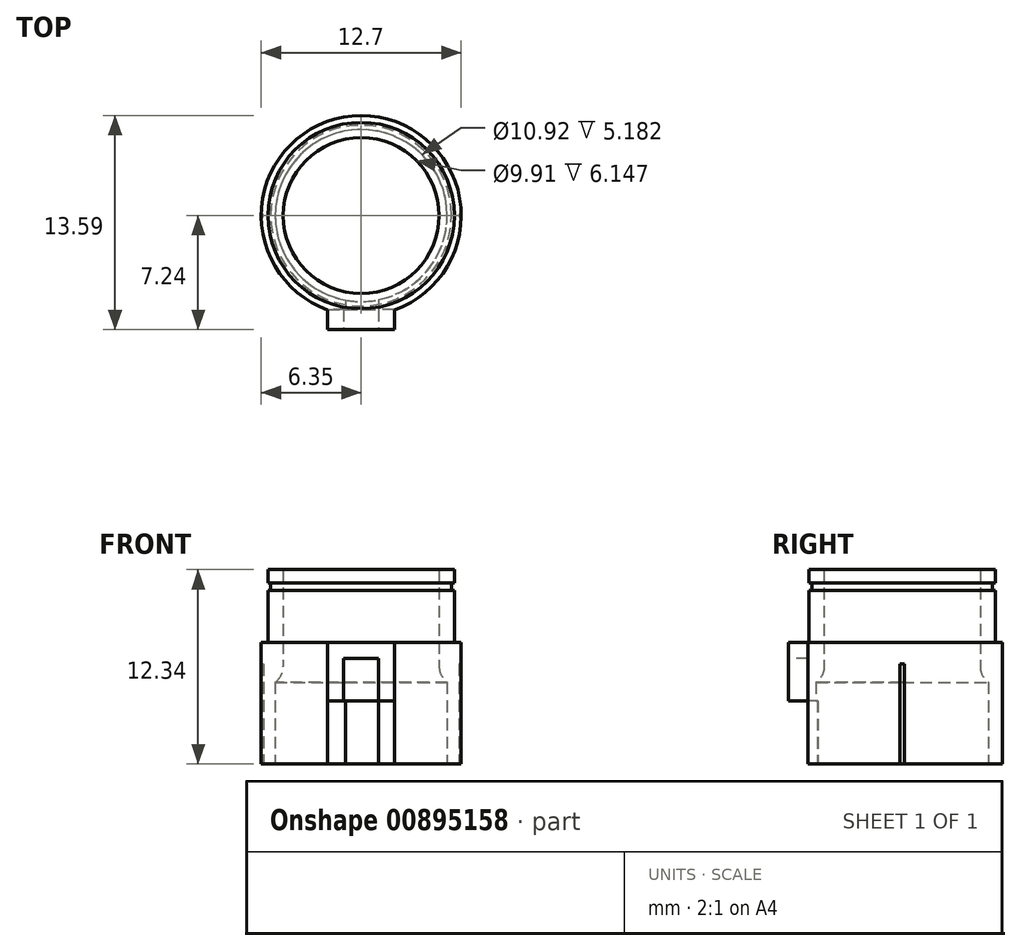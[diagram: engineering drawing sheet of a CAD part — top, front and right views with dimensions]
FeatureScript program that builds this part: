
annotation { "Feature Type Name" : "Feature", "Feature Type Description" : "" }
export const myFeature = defineFeature(function(context is Context, id is Id, definition is map)
    precondition{}
    {
        {
            var Q0;
            Q0=qCreatedBy(makeId("Top.planeOp"),FACE);
            var sketch = newSketch(context, id + "F0", { "sketchPlane" : qUnion([Q0])});
            skCircle(sketch, "E0", {"center": v(0, 0) * mm, "radius": 6.35 * mm});
            skLineSegment(sketch, "E1.bottom", {"start": v(2.12, -5.46) * mm, "end": v(-2.12, -5.46) * mm});
            skLineSegment(sketch, "E1.top", {"start": v(2.12, -7.24) * mm, "end": v(-2.12, -7.24) * mm});
            skLineSegment(sketch, "E1.left", {"start": v(2.12, -5.46) * mm, "end": v(2.12, -7.24) * mm});
            skLineSegment(sketch, "E1.right", {"start": v(-2.12, -5.46) * mm, "end": v(-2.12, -7.24) * mm});
            skPoint(sketch, "E1.middle", {"position": v(0, -6.35) * mm});
            skCircle(sketch, "E2", {"center": v(0, 0) * mm, "radius": 5.46 * mm});
            skSolve(sketch);
        }
        {
            var Q0;
            {var subQ5=sQuery(id+"F0.wireOp",EDGE,"E1.top");Q0=makeQuery(id+"F0.imprint","IMPRINT",FACE,{"disambiguationData":[TD([[makeQuery(id+"F0.imprint","IMPRINT",EDGE,{"derivedFrom":subQ5}),-1.0]])]});}
            var Q1;
            {var subQ4=sQuery(id+"F0.wireOp",EDGE,"E1.left");var subQ6=sQuery(id+"F0.wireOp",EDGE,"E0");var subQ7=makeQuery(id+"F0.imprint","INTERSECT",VERTEX,{"derivedFrom":[subQ6,subQ4]});Q1=makeQuery(id+"F0.imprint","IMPRINT",FACE,{"disambiguationData":[TD([[makeQuery(id+"F0.imprint","IMPRINT",EDGE,{"disambiguationData":[TD([[subQ7,1.0]])],"derivedFrom":subQ6}),1.0]])]});}
            var Q2;
            {var subQ7=sQuery(id+"F0.wireOp",EDGE,"E2");Q2=makeQuery(id+"F0.imprint","IMPRINT",FACE,{"disambiguationData":[TD([[makeQuery(id+"F0.imprint","IMPRINT",EDGE,{"derivedFrom":subQ7}),-1.0]])]});}
            extrude(context, id + "F1", {"entities" : qUnion([Q0, Q1, Q2]), "depth" : 7.72 * mm, "offsetDistance" : 25.4 * mm});
        }
        {
            var Q0;
            Q0=makeQuery(id+"F1.opExtrude","SWEPT_FACE",FACE,{"disambiguationData":[OSD([sQuery(id+"F0.wireOp",EDGE,"E1.top")])]});
            var sketch = newSketch(context, id + "F2", { "sketchPlane" : qUnion([Q0])});
            skLineSegment(sketch, "E3.bottom", {"start": v(-1.1, 0) * mm, "end": v(1.1, 0) * mm});
            skLineSegment(sketch, "E3.top", {"start": v(-1.1, 6.7) * mm, "end": v(1.1, 6.7) * mm});
            skLineSegment(sketch, "E3.left", {"start": v(-1.1, 0) * mm, "end": v(-1.1, 6.7) * mm});
            skLineSegment(sketch, "E3.right", {"start": v(1.1, 0) * mm, "end": v(1.1, 6.7) * mm});
            skLineSegment(sketch, "E4.bottom", {"start": v(-2.12, 4.01) * mm, "end": v(2.12, 4.01) * mm});
            skLineSegment(sketch, "E4.top", {"start": v(-2.12, 0) * mm, "end": v(2.12, 0) * mm});
            skLineSegment(sketch, "E4.left", {"start": v(-2.12, 4.01) * mm, "end": v(-2.12, 0) * mm});
            skLineSegment(sketch, "E4.right", {"start": v(2.12, 4.01) * mm, "end": v(2.12, 0) * mm});
            skSolve(sketch);
        }
        {
            var Q0;
            Q0 = qSketchRegion(id + "F2", true);
            extrude(context, id + "F3", {"entities" : qUnion([Q0]), "operationType" : NewBodyOperationType.REMOVE, "oppositeDirection" : true, "depth" : 1.27 * mm, "offsetDistance" : 25.4 * mm});
        }
        {
            var Q0;
            Q0=makeQuery(id+"F1.opExtrude","CAP_FACE",FACE,{"disambiguationData":[OSD([sQuery(id+"F0.wireOp",EDGE,"E0"),sQuery(id+"F0.wireOp",EDGE,"E1.top"),sQuery(id+"F0.wireOp",EDGE,"E1.left"),sQuery(id+"F0.wireOp",EDGE,"E1.right"),sQuery(id+"F0.wireOp",EDGE,"E2")])],"isStart":true});
            var sketch = newSketch(context, id + "F4", { "sketchPlane" : qUnion([Q0])});
            skCircle(sketch, "E5", {"center": v(-6.35, 0) * mm, "radius": 0.14 * mm});
            skCircle(sketch, "E6", {"center": v(6.35, 0) * mm, "radius": 0.14 * mm});
            skSolve(sketch);
        }
        {
            var Q0;
            {var subQ0=sQuery(id+"F4.wireOp",EDGE,"E6");var subQ1=makeQuery(id+"F1.opExtrude","CAP_EDGE",EDGE,{"disambiguationData":[OSD([sQuery(id+"F0.wireOp",EDGE,"E0")])],"isStart":true});var subQ2=makeQuery(id+"F4.imprint","INTERSECT",VERTEX,{"disambiguationData":[OD(0.0)],"derivedFrom":[subQ1,subQ0]});Q0=makeQuery(id+"F4.imprint","IMPRINT",FACE,{"disambiguationData":[TD([[makeQuery(id+"F4.imprint","IMPRINT",EDGE,{"disambiguationData":[TD([[subQ2,1.0]])],"derivedFrom":subQ0}),1.0]])]});}
            var Q1;
            {var subQ0=sQuery(id+"F4.wireOp",EDGE,"E6");var subQ1=makeQuery(id+"F1.opExtrude","CAP_EDGE",EDGE,{"disambiguationData":[OSD([sQuery(id+"F0.wireOp",EDGE,"E0")])],"isStart":true});var subQ2=makeQuery(id+"F4.imprint","INTERSECT",VERTEX,{"disambiguationData":[OD(0.0)],"derivedFrom":[subQ1,subQ0]});Q1=makeQuery(id+"F4.imprint","IMPRINT",FACE,{"disambiguationData":[TD([[makeQuery(id+"F4.imprint","IMPRINT",EDGE,{"disambiguationData":[TD([[subQ2,-1.0]])],"derivedFrom":subQ0}),1.0]])]});}
            var Q2;
            {var subQ0=sQuery(id+"F4.wireOp",EDGE,"E5");var subQ1=makeQuery(id+"F1.opExtrude","CAP_EDGE",EDGE,{"disambiguationData":[OSD([sQuery(id+"F0.wireOp",EDGE,"E0")])],"isStart":true});var subQ2=makeQuery(id+"F4.imprint","INTERSECT",VERTEX,{"disambiguationData":[OD(0.0)],"derivedFrom":[subQ1,subQ0]});Q2=makeQuery(id+"F4.imprint","IMPRINT",FACE,{"disambiguationData":[TD([[makeQuery(id+"F4.imprint","IMPRINT",EDGE,{"disambiguationData":[TD([[subQ2,1.0]])],"derivedFrom":subQ0}),1.0]])]});}
            var Q3;
            {var subQ0=sQuery(id+"F4.wireOp",EDGE,"E5");var subQ1=makeQuery(id+"F1.opExtrude","CAP_EDGE",EDGE,{"disambiguationData":[OSD([sQuery(id+"F0.wireOp",EDGE,"E0")])],"isStart":true});var subQ2=makeQuery(id+"F4.imprint","INTERSECT",VERTEX,{"disambiguationData":[OD(0.0)],"derivedFrom":[subQ1,subQ0]});Q3=makeQuery(id+"F4.imprint","IMPRINT",FACE,{"disambiguationData":[TD([[makeQuery(id+"F4.imprint","IMPRINT",EDGE,{"disambiguationData":[TD([[subQ2,-1.0]])],"derivedFrom":subQ0}),1.0]])]});}
            extrude(context, id + "F5", {"entities" : qUnion([Q0, Q1, Q2, Q3]), "operationType" : NewBodyOperationType.REMOVE, "oppositeDirection" : true, "depth" : 6.35 * mm, "offsetDistance" : 25.4 * mm});
        }
        {
            var Q0;
            Q0=makeQuery(id+"F1.opExtrude","CAP_FACE",FACE,{"disambiguationData":[OSD([sQuery(id+"F0.wireOp",EDGE,"E0"),sQuery(id+"F0.wireOp",EDGE,"E1.top"),sQuery(id+"F0.wireOp",EDGE,"E1.left"),sQuery(id+"F0.wireOp",EDGE,"E1.right"),sQuery(id+"F0.wireOp",EDGE,"E2")])],"isStart":false});
            var sketch = newSketch(context, id + "F6", { "sketchPlane" : qUnion([Q0])});
            skCircle(sketch, "E7", {"center": v(0, 0) * mm, "radius": 5.92 * mm});
            skCircle(sketch, "E8", {"center": v(0, 0) * mm, "radius": 4.95 * mm});
            skSolve(sketch);
        }
        {
            var Q0;
            Q0 = qSketchRegion(id + "F6", true);
            extrude(context, id + "F7", {"entities" : qUnion([Q0]), "operationType" : NewBodyOperationType.ADD, "depth" : 4.62 * mm, "offsetDistance" : 25.4 * mm, "hasSecondDirection" : true, "secondDirectionOppositeDirection" : true, "secondDirectionDepth" : 2.54 * mm});
        }
        {
            var Q0;
            Q0=makeQuery(id+"F7.opExtrude","CAP_FACE",FACE,{"disambiguationData":[OSD([sQuery(id+"F6.wireOp",EDGE,"E7"),sQuery(id+"F6.wireOp",EDGE,"E8")])],"isStart":false});
            var sketch = newSketch(context, id + "F8", { "sketchPlane" : qUnion([Q0])});
            skCircle(sketch, "E9", {"center": v(0, 0) * mm, "radius": 6.13 * mm});
            skCircle(sketch, "E10", {"center": v(0, 0) * mm, "radius": 5.74 * mm});
            skSolve(sketch);
        }
        {
            var Q0;
            Q0=makeQuery(id+"F8.imprint","IMPRINT",FACE,{"disambiguationData":[TD([[makeQuery(id+"F8.imprint","IMPRINT",EDGE,{"derivedFrom":sQuery(id+"F8.wireOp",EDGE,"E10")}),-1.0]])]});
            var Q1;
            Q1=makeQuery(id+"F8.imprint","IMPRINT",FACE,{"disambiguationData":[TD([[makeQuery(id+"F8.imprint","IMPRINT",EDGE,{"derivedFrom":makeQuery(id+"F7.opExtrude","CAP_EDGE",EDGE,{"disambiguationData":[OSD([sQuery(id+"F6.wireOp",EDGE,"E8")])],"isStart":false})}),1.0]])]});
            extrude(context, id + "F9", {"entities" : qUnion([Q0, Q1]), "operationType" : NewBodyOperationType.REMOVE, "oppositeDirection" : true, "depth" : 1.32 * mm, "offsetDistance" : 25.4 * mm, "hasSecondDirection" : true, "secondDirectionOppositeDirection" : true, "secondDirectionDepth" : 0.84 * mm});
        }
        {
            var Q0;
            Q0=makeQuery(id+"F7.opExtrude","CAP_EDGE",EDGE,{"disambiguationData":[OSD([sQuery(id+"F6.wireOp",EDGE,"E8")])],"isStart":true});
            fillet(context, id + "F10", {"entities" : qUnion([Q0]), "radius" : 1.27 * mm, "tangentPropagation" : true, "allowEdgeOverflow" : false});
        }
        {
            var Q0;
            Q0=makeQuery(id+"F3.boolean.opBoolean","COPY",FACE,{"derivedFrom":makeQuery(id+"F3.opExtrude","CAP_FACE",FACE,{"disambiguationData":[OSD([sQuery(id+"F2.wireOp",EDGE,"E3.top"),sQuery(id+"F2.wireOp",EDGE,"E3.left"),sQuery(id+"F2.wireOp",EDGE,"E3.right"),sQuery(id+"F2.wireOp",EDGE,"E4.bottom"),sQuery(id+"F2.wireOp",EDGE,"E4.top"),sQuery(id+"F2.wireOp",EDGE,"E4.left"),sQuery(id+"F2.wireOp",EDGE,"E4.right")])],"isStart":false})});
            var sketch = newSketch(context, id + "F11", { "sketchPlane" : qUnion([Q0])});
            skLineSegment(sketch, "E11.bottom", {"start": v(-0.99, 0) * mm, "end": v(1.1, 0) * mm});
            skLineSegment(sketch, "E11.top", {"start": v(-0.99, 4.01) * mm, "end": v(1.1, 4.01) * mm});
            skLineSegment(sketch, "E11.left", {"start": v(-0.99, 0) * mm, "end": v(-0.99, 4.01) * mm});
            skLineSegment(sketch, "E11.right", {"start": v(1.1, 0) * mm, "end": v(1.1, 4.01) * mm});
            skSolve(sketch);
        }
        {
            var Q0;
            Q0=makeQuery(id+"F11.imprint","IMPRINT",FACE,{"disambiguationData":[TD([[makeQuery(id+"F11.imprint","IMPRINT",EDGE,{"derivedFrom":sQuery(id+"F11.wireOp",EDGE,"E11.bottom")}),-1.0]])]});
            extrude(context, id + "F12", {"entities" : qUnion([Q0]), "operationType" : NewBodyOperationType.REMOVE, "endBound" : BoundingType.UP_TO_NEXT, "oppositeDirection" : true, "depth" : 25.4 * mm, "offsetDistance" : 25.4 * mm});
        }
    });
